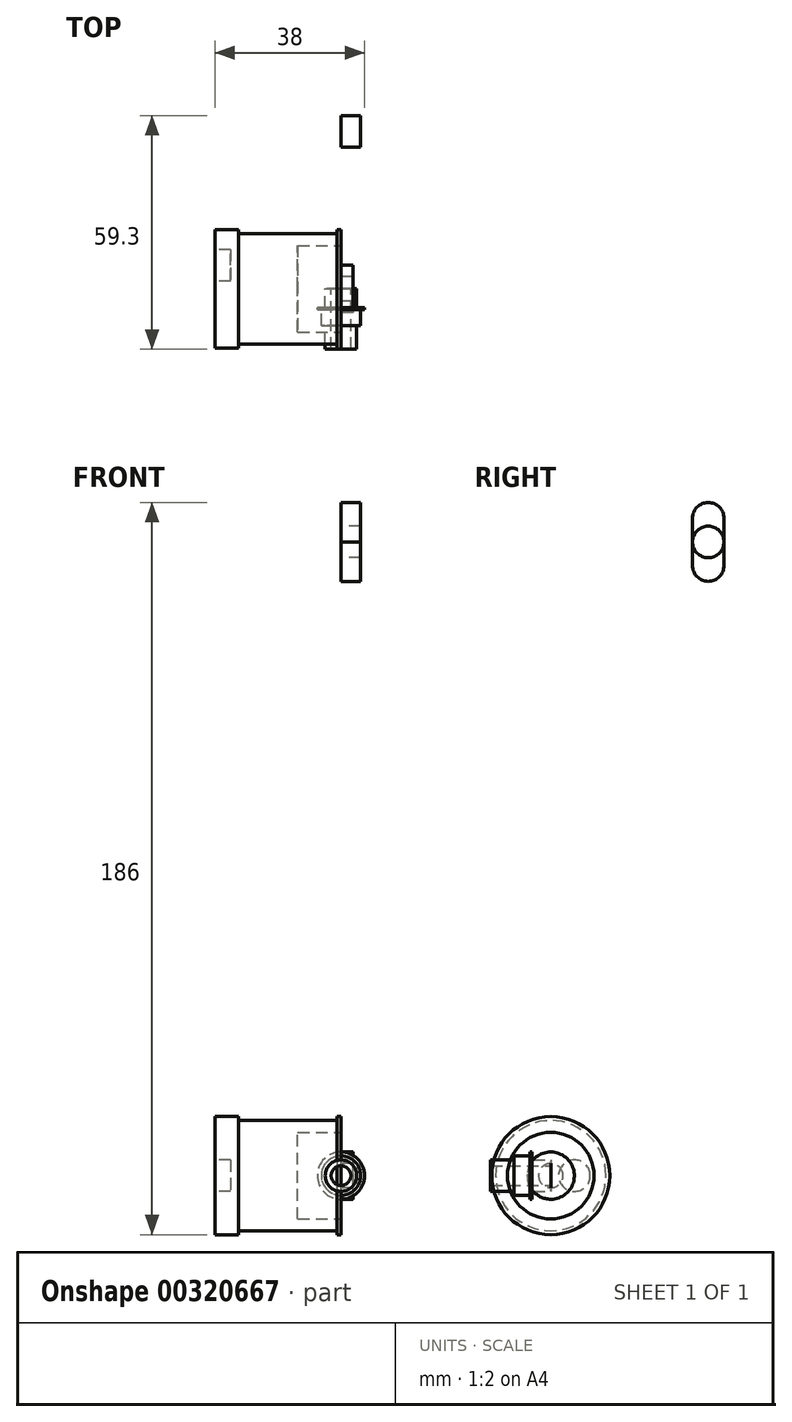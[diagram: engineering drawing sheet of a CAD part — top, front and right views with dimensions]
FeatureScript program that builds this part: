
annotation { "Feature Type Name" : "Feature", "Feature Type Description" : "" }
export const myFeature = defineFeature(function(context is Context, id is Id, definition is map)
    precondition{}
    {
        {
            var Q0;
            Q0=qCreatedBy(makeId("Right.planeOp"),FACE);
            var sketch = newSketch(context, id + "F0", { "sketchPlane" : qUnion([Q0])});
            skArc(sketch, "E0", {"start": v(26, 40) * mm, "mid": v(33, 27.88) * mm, "end": v(47, 27.88) * mm, "construction": true});
            skArc(sketch, "E1", {"start": v(47, 173.12) * mm, "mid": v(33, 173.12) * mm, "end": v(26, 161) * mm, "construction": true});
            skArc(sketch, "E2", {"start": v(151.79, 88.38) * mm, "mid": v(158.79, 100.5) * mm, "end": v(151.79, 112.62) * mm, "construction": true});
            skLineSegment(sketch, "E3", {"start": v(26, 40) * mm, "end": v(26, 161) * mm, "construction": true});
            skLineSegment(sketch, "E4", {"start": v(47, 173.12) * mm, "end": v(151.79, 112.62) * mm, "construction": true});
            skLineSegment(sketch, "E5", {"start": v(47, 27.88) * mm, "end": v(151.79, 88.38) * mm, "construction": true});
            skLineSegment(sketch, "E6", {"start": v(144.79, 100.5) * mm, "end": v(40, 100.5) * mm, "construction": true});
            skLineSegment(sketch, "E7", {"start": v(40, 100.5) * mm, "end": v(40, 161) * mm, "construction": true});
            skLineSegment(sketch, "E8", {"start": v(40, 100.5) * mm, "end": v(40, 40) * mm, "construction": true});
            skLineSegment(sketch, "E9.bottom", {"start": v(20, 0) * mm, "end": v(330, 0) * mm});
            skLineSegment(sketch, "E9.top", {"start": v(20, 200) * mm, "end": v(64.96, 200) * mm});
            skLineSegment(sketch, "E9.left", {"start": v(0, 20) * mm, "end": v(0, 75.5) * mm});
            skLineSegment(sketch, "E9.right", {"start": v(350, 20) * mm, "end": v(350, 120.57) * mm});
            skLineSegment(sketch, "E10.bottom", {"start": v(0, 125.5) * mm, "end": v(106, 125.5) * mm});
            skLineSegment(sketch, "E10.top", {"start": v(0, 75.5) * mm, "end": v(106, 75.5) * mm});
            skLineSegment(sketch, "E10.right", {"start": v(120, 111.5) * mm, "end": v(120, 89.5) * mm});
            skLineSegment(sketch, "E11.trimOffspring", {"start": v(0, 125.5) * mm, "end": v(0, 180) * mm});
            skLineSegment(sketch, "E12", {"start": v(69.33, 199.52) * mm, "end": v(334.38, 140.08) * mm});
            skPoint(sketch, "E13.visualSharp", {"position": v(0, 200) * mm});
            skArc(sketch, "E13.filletArc", {"start": v(20, 200) * mm, "mid": v(5.86, 194.14) * mm, "end": v(0, 180) * mm});
            skPoint(sketch, "E14.visualSharp", {"position": v(0, 0) * mm});
            skArc(sketch, "E14.filletArc", {"start": v(0, 20) * mm, "mid": v(5.86, 5.86) * mm, "end": v(20, 0) * mm});
            skPoint(sketch, "E15.visualSharp", {"position": v(350, 0) * mm});
            skArc(sketch, "E15.filletArc", {"start": v(330, 0) * mm, "mid": v(344.14, 5.86) * mm, "end": v(350, 20) * mm});
            skPoint(sketch, "E16.visualSharp", {"position": v(350, 136.58) * mm});
            skArc(sketch, "E16.filletArc", {"start": v(350, 120.57) * mm, "mid": v(345.61, 133.07) * mm, "end": v(334.38, 140.08) * mm});
            skPoint(sketch, "E17.visualSharp", {"position": v(67.17, 200) * mm});
            skArc(sketch, "E17.filletArc", {"start": v(69.33, 199.52) * mm, "mid": v(67.16, 199.88) * mm, "end": v(64.96, 200) * mm});
            skPoint(sketch, "E18.visualSharp", {"position": v(120, 125.5) * mm});
            skArc(sketch, "E18.filletArc", {"start": v(120, 111.5) * mm, "mid": v(115.9, 121.4) * mm, "end": v(106, 125.5) * mm});
            skPoint(sketch, "E19.visualSharp", {"position": v(120, 75.5) * mm});
            skArc(sketch, "E19.filletArc", {"start": v(106, 75.5) * mm, "mid": v(115.9, 79.6) * mm, "end": v(120, 89.5) * mm});
            skArc(sketch, "E20", {"start": v(312.86, 86.84) * mm, "mid": v(323.8, 100.5) * mm, "end": v(312.86, 114.16) * mm, "construction": true});
            skLineSegment(sketch, "E21", {"start": v(43.06, 174.66) * mm, "end": v(312.86, 114.16) * mm, "construction": true});
            skLineSegment(sketch, "E22", {"start": v(312.86, 86.84) * mm, "end": v(43.06, 26.34) * mm, "construction": true});
            skSolve(sketch);
        }
        {
            var Q0;
            {var subQ1=sQuery(id+"F0.wireOp",EDGE,"E0");Q0=makeQuery(id+"F0.imprint","IMPRINT",FACE,{"disambiguationData":[TD([[makeQuery(id+"F0.imprint","IMPRINT",EDGE,{"derivedFrom":subQ1}),-1.0]])]});}
            var Q1;
            {var subQ8=sQuery(id+"F0.wireOp",EDGE,"E0");Q1=makeQuery(id+"F0.imprint","IMPRINT",FACE,{"disambiguationData":[TD([[makeQuery(id+"F0.imprint","IMPRINT",EDGE,{"derivedFrom":subQ8}),1.0]])]});}
            var Q2;
            Q2=makeQuery(id+"F0.imprint","IMPRINT",FACE,{"disambiguationData":[TD([[makeQuery(id+"F0.imprint","IMPRINT",EDGE,{"derivedFrom":sQuery(id+"F0.wireOp",EDGE,"E1")}),-1.0]])]});
            var Q3;
            Q3=makeQuery(id+"F0.imprint","IMPRINT",FACE,{"disambiguationData":[TD([[makeQuery(id+"F0.imprint","IMPRINT",EDGE,{"derivedFrom":sQuery(id+"F0.wireOp",EDGE,"E9.bottom")}),1.0]])]});
            extrude(context, id + "F1", {"entities" : qUnion([Q0, Q1, Q2, Q3]), "depth" : 5 * mm});
        }
        {
            var Q0;
            Q0=sQuery(id+"F0.wireOp",VERTEX,"E2.center");
            var Q1;
            Q1=sQuery(id+"F0.wireOp",VERTEX,"E20.center");
            var Q2;
            Q2=sQuery(id+"F0.wireOp",VERTEX,"E1.center");
            var Q3;
            Q3=sQuery(id+"F0.wireOp",VERTEX,"E0.center");
            var Q4;
            Q4=makeQuery(id+"F1.opExtrude","SWEPT_BODY",BODY,{"disambiguationData":[OSD([sQuery(id+"F0.wireOp",EDGE,"E9.bottom"),sQuery(id+"F0.wireOp",EDGE,"E9.top"),sQuery(id+"F0.wireOp",EDGE,"E9.left"),sQuery(id+"F0.wireOp",EDGE,"E9.right"),sQuery(id+"F0.wireOp",EDGE,"E10.bottom"),sQuery(id+"F0.wireOp",EDGE,"E10.top"),sQuery(id+"F0.wireOp",EDGE,"E10.right"),sQuery(id+"F0.wireOp",EDGE,"E11.trimOffspring"),sQuery(id+"F0.wireOp",EDGE,"E12"),sQuery(id+"F0.wireOp",EDGE,"E13.filletArc"),sQuery(id+"F0.wireOp",EDGE,"E14.filletArc"),sQuery(id+"F0.wireOp",EDGE,"E15.filletArc"),sQuery(id+"F0.wireOp",EDGE,"E16.filletArc"),sQuery(id+"F0.wireOp",EDGE,"E17.filletArc"),sQuery(id+"F0.wireOp",EDGE,"E18.filletArc"),sQuery(id+"F0.wireOp",EDGE,"E19.filletArc")])]});
            hole(context, id + "F2", {"style" : HoleStyle.SIMPLE, "endStyle" : HoleEndStyle.THROUGH, "oppositeDirection" : true, "standardTappedOrClearance" : lookupTablePath({ "standard" : "ISO", "size" : "8", "type" : "Drilled" }), "standardBlindInLast" : lookupTablePath({ "standard" : "ISO", "size" : "8", "type" : "Drilled" }), "holeDiameter" : 8 * mm, "tappedDepth" : 12 * mm, "tapClearance" : 3, "startFromSketch" : true, "locations" : qUnion([Q0, Q1, Q2, Q3]), "scope" : qUnion([Q4])});
        }
        {
            var Q0;
            Q0=makeQuery(id+"F1.opExtrude","CAP_FACE",FACE,{"disambiguationData":[OSD([sQuery(id+"F0.wireOp",EDGE,"E9.bottom"),sQuery(id+"F0.wireOp",EDGE,"E9.top"),sQuery(id+"F0.wireOp",EDGE,"E9.left"),sQuery(id+"F0.wireOp",EDGE,"E9.right"),sQuery(id+"F0.wireOp",EDGE,"E10.bottom"),sQuery(id+"F0.wireOp",EDGE,"E10.top"),sQuery(id+"F0.wireOp",EDGE,"E10.right"),sQuery(id+"F0.wireOp",EDGE,"E11.trimOffspring"),sQuery(id+"F0.wireOp",EDGE,"E12"),sQuery(id+"F0.wireOp",EDGE,"E13.filletArc"),sQuery(id+"F0.wireOp",EDGE,"E14.filletArc"),sQuery(id+"F0.wireOp",EDGE,"E15.filletArc"),sQuery(id+"F0.wireOp",EDGE,"E16.filletArc"),sQuery(id+"F0.wireOp",EDGE,"E17.filletArc"),sQuery(id+"F0.wireOp",EDGE,"E18.filletArc"),sQuery(id+"F0.wireOp",EDGE,"E19.filletArc")])],"isStart":false});
            var sketch = newSketch(context, id + "F3", { "sketchPlane" : qUnion([Q0])});
            skLineSegment(sketch, "E23.left", {"start": v(44, 155) * mm, "end": v(44, 167) * mm});
            skLineSegment(sketch, "E23.right", {"start": v(36, 155) * mm, "end": v(36, 167) * mm});
            skPoint(sketch, "E23.middle", {"position": v(40, 161) * mm});
            skArc(sketch, "E24", {"start": v(36, 167) * mm, "mid": v(40, 171) * mm, "end": v(44, 167) * mm});
            skArc(sketch, "E25", {"start": v(44, 155) * mm, "mid": v(40, 151) * mm, "end": v(36, 155) * mm});
            skSolve(sketch);
        }
        {
            var Q0;
            {var subQ0=sQuery(id+"F3.wireOp",EDGE,"E24");Q0=makeQuery(id+"F3.imprint","IMPRINT",FACE,{"disambiguationData":[TD([[makeQuery(id+"F3.imprint","IMPRINT",EDGE,{"derivedFrom":subQ0}),-1.0]])]});}
            var Q1;
            {var subQ0=sQuery(id+"F3.wireOp",EDGE,"E25");Q1=makeQuery(id+"F3.imprint","IMPRINT",FACE,{"disambiguationData":[TD([[makeQuery(id+"F3.imprint","IMPRINT",EDGE,{"derivedFrom":subQ0}),-1.0]])]});}
            extrude(context, id + "F4", {"entities" : qUnion([Q0, Q1]), "operationType" : NewBodyOperationType.REMOVE, "endBound" : BoundingType.THROUGH_ALL, "oppositeDirection" : true, "depth" : 25 * mm});
        }
        {
            var Q0;
            Q0=qCreatedBy(makeId("Right.planeOp"),FACE);
            var sketch = newSketch(context, id + "F5", { "sketchPlane" : qUnion([Q0])});
            skCircle(sketch, "E26", {"center": v(0, 0) * mm, "radius": 15 * mm});
            skSolve(sketch);
        }
        {
            var Q0;
            Q0=makeQuery(id+"F5.imprint","IMPRINT",FACE,{"disambiguationData":[TD([[makeQuery(id+"F5.imprint","IMPRINT",EDGE,{"derivedFrom":sQuery(id+"F5.wireOp",EDGE,"E26")}),1.0]])]});
            extrude(context, id + "F6", {"entities" : qUnion([Q0]), "oppositeDirection" : true, "depth" : 1 * mm});
        }
        {
            var Q0;
            Q0=makeQuery(id+"F6.opExtrude","CAP_FACE",FACE,{"disambiguationData":[OSD([sQuery(id+"F5.wireOp",EDGE,"E26")])],"isStart":false});
            var sketch = newSketch(context, id + "F7", { "sketchPlane" : qUnion([Q0])});
            skCircle(sketch, "E27", {"center": v(0, 0) * mm, "radius": 14 * mm});
            skSolve(sketch);
        }
        {
            var Q0;
            Q0=makeQuery(id+"F7.imprint","IMPRINT",FACE,{"disambiguationData":[TD([[makeQuery(id+"F7.imprint","IMPRINT",EDGE,{"derivedFrom":sQuery(id+"F7.wireOp",EDGE,"E27")}),1.0]])]});
            extrude(context, id + "F8", {"entities" : qUnion([Q0]), "operationType" : NewBodyOperationType.ADD, "depth" : 25 * mm});
        }
        {
            var Q0;
            Q0=makeQuery(id+"F8.opExtrude","CAP_FACE",FACE,{"disambiguationData":[OSD([sQuery(id+"F7.wireOp",EDGE,"E27")])],"isStart":false});
            var sketch = newSketch(context, id + "F9", { "sketchPlane" : qUnion([Q0])});
            skCircle(sketch, "E28", {"center": v(0, 0) * mm, "radius": 15 * mm});
            skSolve(sketch);
        }
        {
            var Q0;
            Q0=makeQuery(id+"F9.imprint","IMPRINT",FACE,{"disambiguationData":[TD([[makeQuery(id+"F9.imprint","IMPRINT",EDGE,{"derivedFrom":makeQuery(id+"F8.opExtrude","CAP_EDGE",EDGE,{"disambiguationData":[OSD([sQuery(id+"F7.wireOp",EDGE,"E27")])],"isStart":false})}),1.0]])]});
            var Q1;
            Q1=makeQuery(id+"F9.imprint","IMPRINT",FACE,{"disambiguationData":[TD([[makeQuery(id+"F9.imprint","IMPRINT",EDGE,{"derivedFrom":sQuery(id+"F9.wireOp",EDGE,"E28")}),1.0]])]});
            extrude(context, id + "F10", {"entities" : qUnion([Q0, Q1]), "operationType" : NewBodyOperationType.ADD, "depth" : 6 * mm});
        }
        {
            var Q0;
            Q0=qCreatedBy(makeId("Right.planeOp"),FACE);
            var sketch = newSketch(context, id + "F11", { "sketchPlane" : qUnion([Q0])});
            skCircle(sketch, "E29", {"center": v(0, 0) * mm, "radius": 11 * mm});
            skSolve(sketch);
        }
        {
            var Q0;
            Q0=makeQuery(id+"F11.imprint","IMPRINT",FACE,{"disambiguationData":[TD([[makeQuery(id+"F11.imprint","IMPRINT",EDGE,{"derivedFrom":sQuery(id+"F11.wireOp",EDGE,"E29")}),1.0]])]});
            extrude(context, id + "F12", {"entities" : qUnion([Q0]), "operationType" : NewBodyOperationType.REMOVE, "oppositeDirection" : true, "depth" : 11 * mm});
        }
        {
            var Q0;
            Q0=makeQuery(id+"F10.opExtrude","CAP_FACE",FACE,{"disambiguationData":[OSD([sQuery(id+"F9.wireOp",EDGE,"E28")])],"isStart":false});
            var sketch = newSketch(context, id + "F13", { "sketchPlane" : qUnion([Q0])});
            skCircle(sketch, "E30", {"center": v(-6, 0) * mm, "radius": 4 * mm});
            skSolve(sketch);
        }
        {
            var Q0;
            Q0=makeQuery(id+"F13.imprint","IMPRINT",FACE,{"disambiguationData":[TD([[makeQuery(id+"F13.imprint","IMPRINT",EDGE,{"derivedFrom":sQuery(id+"F13.wireOp",EDGE,"E30")}),1.0]])]});
            extrude(context, id + "F14", {"entities" : qUnion([Q0]), "operationType" : NewBodyOperationType.REMOVE, "oppositeDirection" : true, "depth" : 4 * mm});
        }
        {
            var Q0;
            Q0=qCreatedBy(makeId("Right.planeOp"),FACE);
            var sketch = newSketch(context, id + "F15", { "sketchPlane" : qUnion([Q0])});
            skLineSegment(sketch, "E31", {"start": v(0, -2.5) * mm, "end": v(0, -4) * mm});
            skLineSegment(sketch, "E32", {"start": v(0, -4) * mm, "end": v(-4.8, -4) * mm});
            skLineSegment(sketch, "E33", {"start": v(-4.8, -4) * mm, "end": v(-4.8, -6) * mm});
            skLineSegment(sketch, "E34", {"start": v(-4.8, -6) * mm, "end": v(-5.3, -6) * mm});
            skLineSegment(sketch, "E35", {"start": v(-5.3, -6) * mm, "end": v(-5.3, -5) * mm});
            skLineSegment(sketch, "E36", {"start": v(-5.3, -5) * mm, "end": v(-9.3, -5) * mm});
            skLineSegment(sketch, "E37", {"start": v(-9.3, -5) * mm, "end": v(-9.3, -4) * mm});
            skLineSegment(sketch, "E38", {"start": v(-15.3, -2.5) * mm, "end": v(0, -2.5) * mm});
            skLineSegment(sketch, "E39", {"start": v(-9.3, -4) * mm, "end": v(-15.3, -4) * mm});
            skLineSegment(sketch, "E40", {"start": v(-15.3, -4) * mm, "end": v(-15.3, -2.5) * mm});
            skLineSegment(sketch, "E41", {"start": v(0, 0) * mm, "end": v(-15.3, 0) * mm});
            skSolve(sketch);
        }
        {
            var Q0;
            Q0=makeQuery(id+"F15.imprint","IMPRINT",FACE,{"disambiguationData":[TD([[makeQuery(id+"F15.imprint","IMPRINT",EDGE,{"derivedFrom":sQuery(id+"F15.wireOp",EDGE,"E31")}),-1.0]])]});
            var Q1;
            Q1=sQuery(id+"F15.wireOp",EDGE,"E41");
            revolve(context, id + "F16", {"entities" : qUnion([Q0]), "axis" : qUnion([Q1]), "revolveType" : RevolveType.FULL});
        }
        {
            var Q0;
            Q0=qCreatedBy(makeId("Right.planeOp"),FACE);
            var sketch = newSketch(context, id + "F17", { "sketchPlane" : qUnion([Q0])});
            skCircle(sketch, "E42", {"center": v(0, 0) * mm, "radius": 3.1 * mm});
            skCircle(sketch, "E43", {"center": v(0, 0) * mm, "radius": 6 * mm});
            skSolve(sketch);
        }
        {
            var Q0;
            Q0=makeQuery(id+"F17.imprint","IMPRINT",FACE,{"disambiguationData":[TD([[makeQuery(id+"F17.imprint","IMPRINT",EDGE,{"derivedFrom":sQuery(id+"F17.wireOp",EDGE,"E42")}),-1.0]])]});
            extrude(context, id + "F18", {"entities" : qUnion([Q0]), "depth" : 3 * mm});
        }
    });
